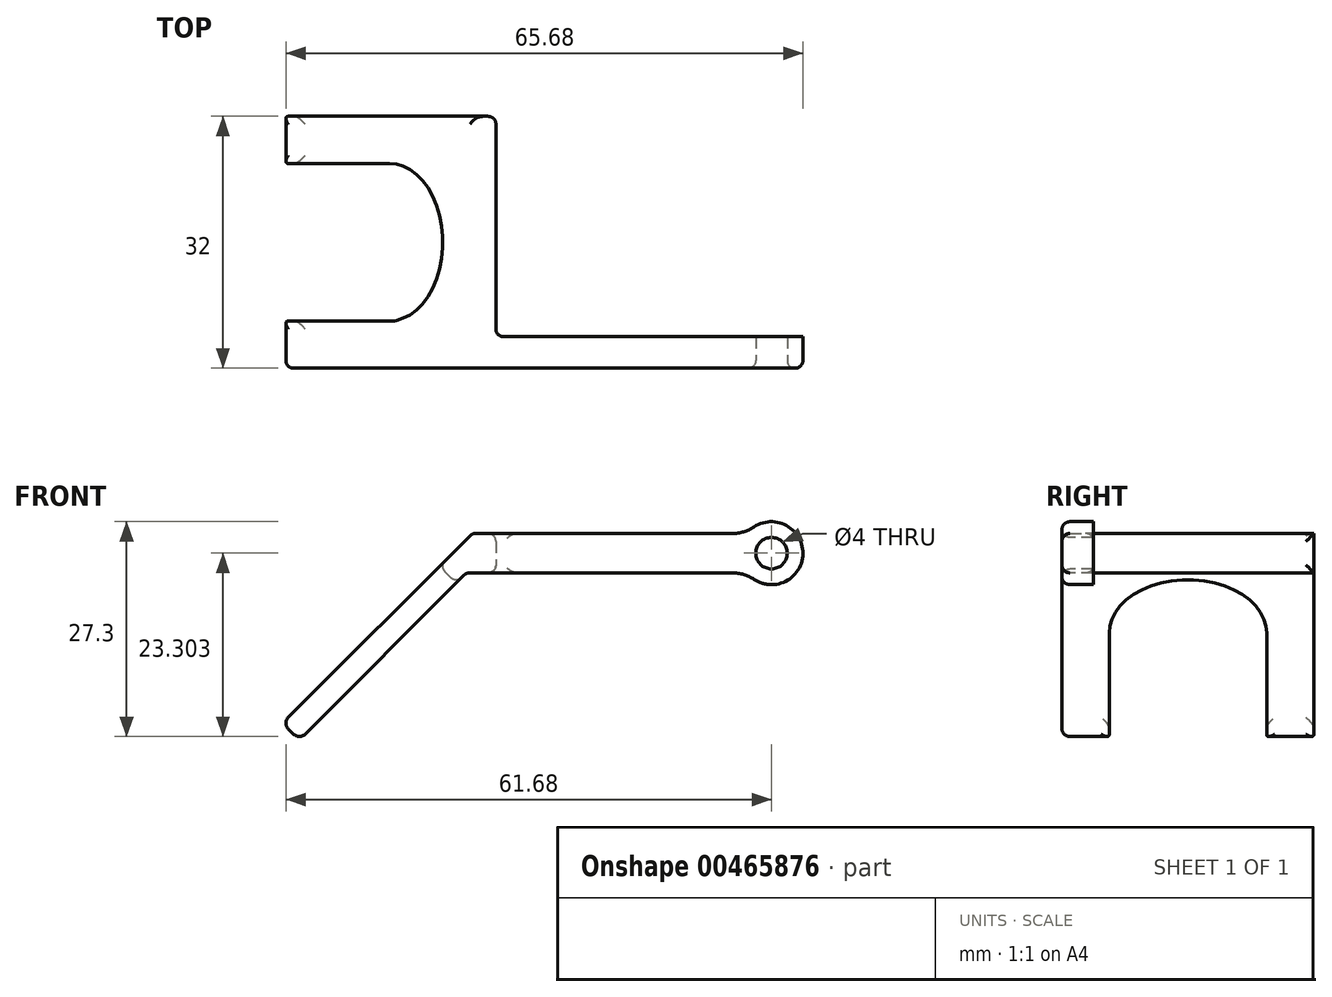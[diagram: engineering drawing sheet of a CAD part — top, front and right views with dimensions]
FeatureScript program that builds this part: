
annotation { "Feature Type Name" : "Feature", "Feature Type Description" : "" }
export const myFeature = defineFeature(function(context is Context, id is Id, definition is map)
    precondition{}
    {
        {
            var Q0;
            Q0=qCreatedBy(makeId("Front.planeOp"),FACE);
            var sketch = newSketch(context, id + "F0", { "sketchPlane" : qUnion([Q0])});
            skLineSegment(sketch, "E0", {"start": v(-24.97, 0) * mm, "end": v(-27.1, 2.12) * mm});
            skLineSegment(sketch, "E1", {"start": v(-27.1, 2.12) * mm, "end": v(-3, 26.21) * mm});
            skLineSegment(sketch, "E2", {"start": v(-3, 26.21) * mm, "end": v(0, 26.21) * mm});
            skLineSegment(sketch, "E3", {"start": v(0, 26.21) * mm, "end": v(0, 21.21) * mm});
            skLineSegment(sketch, "E4", {"start": v(0, 21.21) * mm, "end": v(-3.76, 21.21) * mm});
            skLineSegment(sketch, "E5", {"start": v(-3.76, 21.21) * mm, "end": v(-24.97, 0) * mm});
            skSolve(sketch);
        }
        {
            var Q0;
            Q0=makeQuery(id+"F0.imprint","IMPRINT",FACE,{"disambiguationData":[TD([[makeQuery(id+"F0.imprint","IMPRINT",EDGE,{"derivedFrom":sQuery(id+"F0.wireOp",EDGE,"E0")}),-1.0]])]});
            extrude(context, id + "F1", {"entities" : qUnion([Q0]), "depth" : 32 * mm});
        }
        {
            var Q0;
            Q0=makeQuery(id+"F1.opExtrude","SWEPT_FACE",FACE,{"disambiguationData":[OSD([sQuery(id+"F0.wireOp",EDGE,"E1")])]});
            var sketch = newSketch(context, id + "F2", { "sketchPlane" : qUnion([Q0])});
            skLineSegment(sketch, "E6", {"start": v(6, -17.66) * mm, "end": v(6, 10.54) * mm});
            skLineSegment(sketch, "E7", {"start": v(6, 10.54) * mm, "end": v(26, 10.54) * mm});
            skLineSegment(sketch, "E8", {"start": v(26, 10.54) * mm, "end": v(26, -17.66) * mm});
            skLineSegment(sketch, "E9", {"start": v(26, -17.66) * mm, "end": v(6, -17.66) * mm});
            skSolve(sketch);
        }
        {
            var Q0;
            Q0=makeQuery(id+"F2.imprint","IMPRINT",FACE,{"disambiguationData":[TD([[makeQuery(id+"F2.imprint","IMPRINT",EDGE,{"derivedFrom":sQuery(id+"F2.wireOp",EDGE,"E6")}),-1.0]])]});
            extrude(context, id + "F3", {"entities" : qUnion([Q0]), "operationType" : NewBodyOperationType.REMOVE, "oppositeDirection" : true, "depth" : 3 * mm});
        }
        {
            var Q0;
            Q0=makeQuery(id+"F1.opExtrude","CAP_FACE",FACE,{"disambiguationData":[OSD([sQuery(id+"F0.wireOp",EDGE,"E0"),sQuery(id+"F0.wireOp",EDGE,"E1"),sQuery(id+"F0.wireOp",EDGE,"E2"),sQuery(id+"F0.wireOp",EDGE,"E3"),sQuery(id+"F0.wireOp",EDGE,"E4"),sQuery(id+"F0.wireOp",EDGE,"E5")])],"isStart":false});
            var sketch = newSketch(context, id + "F4", { "sketchPlane" : qUnion([Q0])});
            skLineSegment(sketch, "E10", {"start": v(0, 26.21) * mm, "end": v(30.03, 26.21) * mm});
            skLineSegment(sketch, "E11", {"start": v(0, 26.21) * mm, "end": v(0, 21.21) * mm});
            skLineSegment(sketch, "E12", {"start": v(0, 21.21) * mm, "end": v(30.03, 21.21) * mm});
            skLineSegment(sketch, "E13", {"start": v(0, 23.71) * mm, "end": v(43.19, 23.71) * mm, "construction": true});
            skPoint(sketch, "E13.endSnap0", {"position": v(0, 23.71) * mm});
            skArc(sketch, "E14", {"start": v(32.79, 20.38) * mm, "mid": v(39, 23.71) * mm, "end": v(32.79, 27.05) * mm});
            skArc(sketch, "E15", {"start": v(31.88, 26.21) * mm, "mid": v(31, 23.71) * mm, "end": v(31.88, 21.21) * mm, "construction": true});
            skCircle(sketch, "E16", {"center": v(35, 23.71) * mm, "radius": 2 * mm});
            skPoint(sketch, "E17.visualSharp", {"position": v(31.88, 26.21) * mm});
            skArc(sketch, "E17.filletArc", {"start": v(30.03, 26.21) * mm, "mid": v(31.47, 26.43) * mm, "end": v(32.79, 27.05) * mm});
            skPoint(sketch, "E18.visualSharp", {"position": v(31.88, 21.21) * mm});
            skArc(sketch, "E18.filletArc", {"start": v(32.79, 20.38) * mm, "mid": v(31.47, 21) * mm, "end": v(30.03, 21.21) * mm});
            skSolve(sketch);
        }
        {
            var Q0;
            Q0=makeQuery(id+"F4.imprint","IMPRINT",FACE,{"disambiguationData":[TD([[makeQuery(id+"F4.imprint","IMPRINT",EDGE,{"derivedFrom":sQuery(id+"F4.wireOp",EDGE,"E10")}),-1.0]])]});
            extrude(context, id + "F5", {"entities" : qUnion([Q0]), "operationType" : NewBodyOperationType.ADD, "oppositeDirection" : true, "depth" : 4 * mm});
        }
        {
            var Q0;
            Q0=makeQuery(id+"F3.boolean.opBoolean","COPY",EDGE,{"derivedFrom":makeQuery(id+"F3.opExtrude","SWEPT_EDGE",EDGE,{"disambiguationData":[OSD([sQuery(id+"F2.wireOp",EDGE,"E7"),sQuery(id+"F2.wireOp",EDGE,"E8")])]})});
            var Q1;
            Q1=makeQuery(id+"F3.boolean.opBoolean","COPY",EDGE,{"derivedFrom":makeQuery(id+"F3.opExtrude","SWEPT_EDGE",EDGE,{"disambiguationData":[OSD([sQuery(id+"F2.wireOp",EDGE,"E6"),sQuery(id+"F2.wireOp",EDGE,"E7")])]})});
            fillet(context, id + "F6", {"entities" : qUnion([Q0, Q1]), "radius" : 10 * mm, "tangentPropagation" : true, "allowEdgeOverflow" : false});
        }
        {
            var Q0;
            Q0=makeQuery(id+"F1.opExtrude","CAP_EDGE",EDGE,{"disambiguationData":[OSD([sQuery(id+"F0.wireOp",EDGE,"E1")])],"isStart":false});
            var Q1;
            Q1=makeQuery(id+"F1.opExtrude","SWEPT_EDGE",EDGE,{"disambiguationData":[OSD([sQuery(id+"F0.wireOp",EDGE,"E1"),sQuery(id+"F0.wireOp",EDGE,"E2")])]});
            var Q2;
            Q2=makeQuery(id+"F1.opExtrude","SWEPT_FACE",FACE,{"disambiguationData":[OSD([sQuery(id+"F0.wireOp",EDGE,"E1")])]});
            var Q3;
            Q3=makeQuery(id+"F5.boolean.opBoolean","MERGE",FACE,{"derivedFrom":[makeQuery(id+"F1.opExtrude","CAP_FACE",FACE,{"disambiguationData":[OSD([sQuery(id+"F0.wireOp",EDGE,"E0"),sQuery(id+"F0.wireOp",EDGE,"E1"),sQuery(id+"F0.wireOp",EDGE,"E2"),sQuery(id+"F0.wireOp",EDGE,"E3"),sQuery(id+"F0.wireOp",EDGE,"E4"),sQuery(id+"F0.wireOp",EDGE,"E5")])],"isStart":false}),makeQuery(id+"F5.opExtrude","CAP_FACE",FACE,{"disambiguationData":[OSD([sQuery(id+"F4.wireOp",EDGE,"E10"),sQuery(id+"F4.wireOp",EDGE,"E11"),sQuery(id+"F4.wireOp",EDGE,"E12"),sQuery(id+"F4.wireOp",EDGE,"E14"),sQuery(id+"F4.wireOp",EDGE,"E16"),sQuery(id+"F4.wireOp",EDGE,"E17.filletArc"),sQuery(id+"F4.wireOp",EDGE,"E18.filletArc")])],"isStart":true})]});
            var Q4;
            Q4=makeQuery(id+"F1.opExtrude","SWEPT_FACE",FACE,{"disambiguationData":[OSD([sQuery(id+"F0.wireOp",EDGE,"E5")])]});
            var Q5;
            Q5=makeQuery(id+"F1.opExtrude","SWEPT_FACE",FACE,{"disambiguationData":[OSD([sQuery(id+"F0.wireOp",EDGE,"E3")])]});
            fillet(context, id + "F7", {"entities" : qUnion([Q0, Q1, Q2, Q3, Q4, Q5]), "radius" : 1 * mm, "tangentPropagation" : true, "allowEdgeOverflow" : false});
        }
    });
